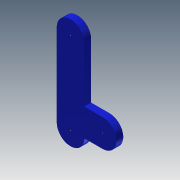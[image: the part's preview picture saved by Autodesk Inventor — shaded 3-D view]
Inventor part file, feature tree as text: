
AUTODESK INVENTOR PART (.ipt)
format: ipt  version: 2013 (Build 170138000, 138)  size: 134,656 bytes
history: native  units: mm
features: extrude x5, sketch x5
ambient origin geometry x8: Origin, YZ Plane, XZ Plane, XY Plane, X Axis, Y Axis, Z Axis, Center Point
bodies: Solid1 (feature_tree)
feature tree (10):
  extrude  "Extrusion1"  Depth=18.0mm
  extrude  "Extrusion2"  Depth=6.0mm
  extrude  "Extrusion3"  Depth=4.0mm
  extrude  "Extrusion4"  Depth=3.0mm
  extrude  "Extrusion5"  Depth=1.5mm TaperAngle=0.0deg
  sketch  "Sketch1"  dims[d0=6.0mm d1=18.0mm]
  sketch  "Sketch2"  dims[d2=6.0mm d4=6.0mm]
  sketch  "Sketch3"  dims[d5=4.0mm d6=4.0mm]
  sketch  "Sketch4"  dims[d7=2.0mm d10=3.0mm]
  sketch  "Sketch5"  dims[d11=6.0mm d12=1.5mm d13=0.0mm d14=3.0mm d15=3.0mm d16=4.0mm d17=6.0mm d18=1.5mm d19=0.0mm d20=4.0mm d21=6.0mm d22=4.0mm d23=1.5mm d24=0.0mm d25=3.0mm d26=1.5mm d27=0.0mm d28=0.2mm d29=0.2mm d30=0.2mm d31=1.5mm d32=0.0mm]
